# Revit family: Haworth_JiveTable_Rectangle_DiscBase
name_source: partatom
category: Furniture Systems
revit_build: Autodesk Revit 2018 (Build: 20170223_1515(x64)
units: mm (PartAtom-declared; Revit-internal decimal feet)

## family parameters
Always vertical = Yes
Cut with Voids When Loaded = No
OmniClass Number = 23.40.70.14.64.21
OmniClass Title = Systems Furniture
Part Type = Normal
Room Calculation Point = No
Round Connector Dimension = Use Diameter
Shared = No
Work Plane-Based = No

## types (13) — shared parameters
Assembly Code = E2020200
Custom Size = No
Manufacturer = Haworth, Inc.
Max. Depth = 42"
Max. Height = 36"
Max. Width = 96"
Min. Depth = 24"
Min. Height = 29"
Min. Width = 24"
Model = Haworth Jive
Revision Number = 0
Size = Verify Final Dim. w/ Haworth
Standard Depths = 24, 30, 36, 42in.
Standard Height = 29, 36 in.
Standard Widths = 24, 30, 36, 42, 60, 72, 84, 96 in.
Table Thickness = 1 3/16"
URL = https://www.haworth.com
URL - Product = https://www.haworth.com
Warranty = http://www.haworth.com

## per-type parameters (varying)
| type | Actual Depth | Actual Height | Actual Width | Base Distance | Depth | Description | Disc Distance | Height | Leg Height | One Disk | Two Disk | Width |
| 24d 24w 29h | 24" | 29" | 24" | 0" | 24" | Haworth Jive Table Rectangle Disc Base - 24d 24w 29h | 8 109/128" | 29" | 27 13/16" | Yes | No | 24" |
| 30d 30w 29h | 30" | 29" | 30" | 0" | 30" | Haworth Jive Table Rectangle Disc Base - 30d 30w 29h | 11" | 29" | 27 13/16" | Yes | No | 30" |
| 36d 36w 29h | 36" | 29" | 36" | 0" | 36" | Haworth Jive Table Rectangle Disc Base - 36d 36w 29h | 13 1/2" | 29" | 27 13/16" | Yes | No | 36" |
| 42d 42w 29h | 42" | 29" | 42" | 0" | 42" | Haworth Jive Table Rectangle Disc Base - 42d 42w 29h | 13 1/2" | 29" | 27 13/16" | Yes | No | 42" |
| 30d 30w 36h | 30" | 36" | 30" | 0" | 30" | Haworth Jive Table Rectangle Disc Base - 30d 30w 36h | 11" | 36" | 34 13/16" | Yes | No | 30" |
| 36d 36w 36h | 36" | 36" | 36" | 0" | 36" | Haworth Jive Table Rectangle Disc Base - 36d 36w 36h | 13 1/2" | 36" | 34 13/16" | Yes | No | 36" |
| 42d 42w 36h | 42" | 36" | 42" | 0" | 42" | Haworth Jive Table Rectangle Disc Base - 42d 42w 36h | 13 1/2" | 36" | 34 13/16" | Yes | No | 42" |
| 30d 60w 29h | 30" | 29" | 60" | 0" | 30" | Haworth Jive Table Rectangle Disc Base - 30d 60w 29h | 13 1/2" | 29" | 27 13/16" | Yes | Yes | 60" |
| 30d 72w 29h | 30" | 29" | 72" | 34" | 30" | Haworth Jive Table Rectangle Disc Base - 30d 72w 29h | 13 1/2" | 29" | 27 13/16" | No | Yes | 72" |
| 36d 72w 29h | 36" | 29" | 72" | 34" | 36" | Haworth Jive Table Rectangle Disc Base - 36d 72w 29h | 13 1/2" | 29" | 27 13/16" | No | Yes | 72" |
| 36d 84w 29h | 36" | 29" | 84" | 46" | 36" | Haworth Jive Table Rectangle Disc Base - 36d 84w 29h | 13 1/2" | 29" | 27 13/16" | No | Yes | 84" |
| 42d 84w 29h | 42" | 29" | 84" | 46" | 42" | Haworth Jive Table Rectangle Disc Base - 42d 84w 29h | 13 1/2" | 29" | 27 13/16" | No | Yes | 84" |
| 42d 96w 29h | 42" | 29" | 96" | 58" | 42" | Haworth Jive Table Rectangle Disc Base - 42d 96w 29h | 13 1/2" | 29" | 27 13/16" | No | Yes | 96" |

## geometry (parser evidence)
native form markers: Sweep x6
no freeform markers — native parametric forms only
